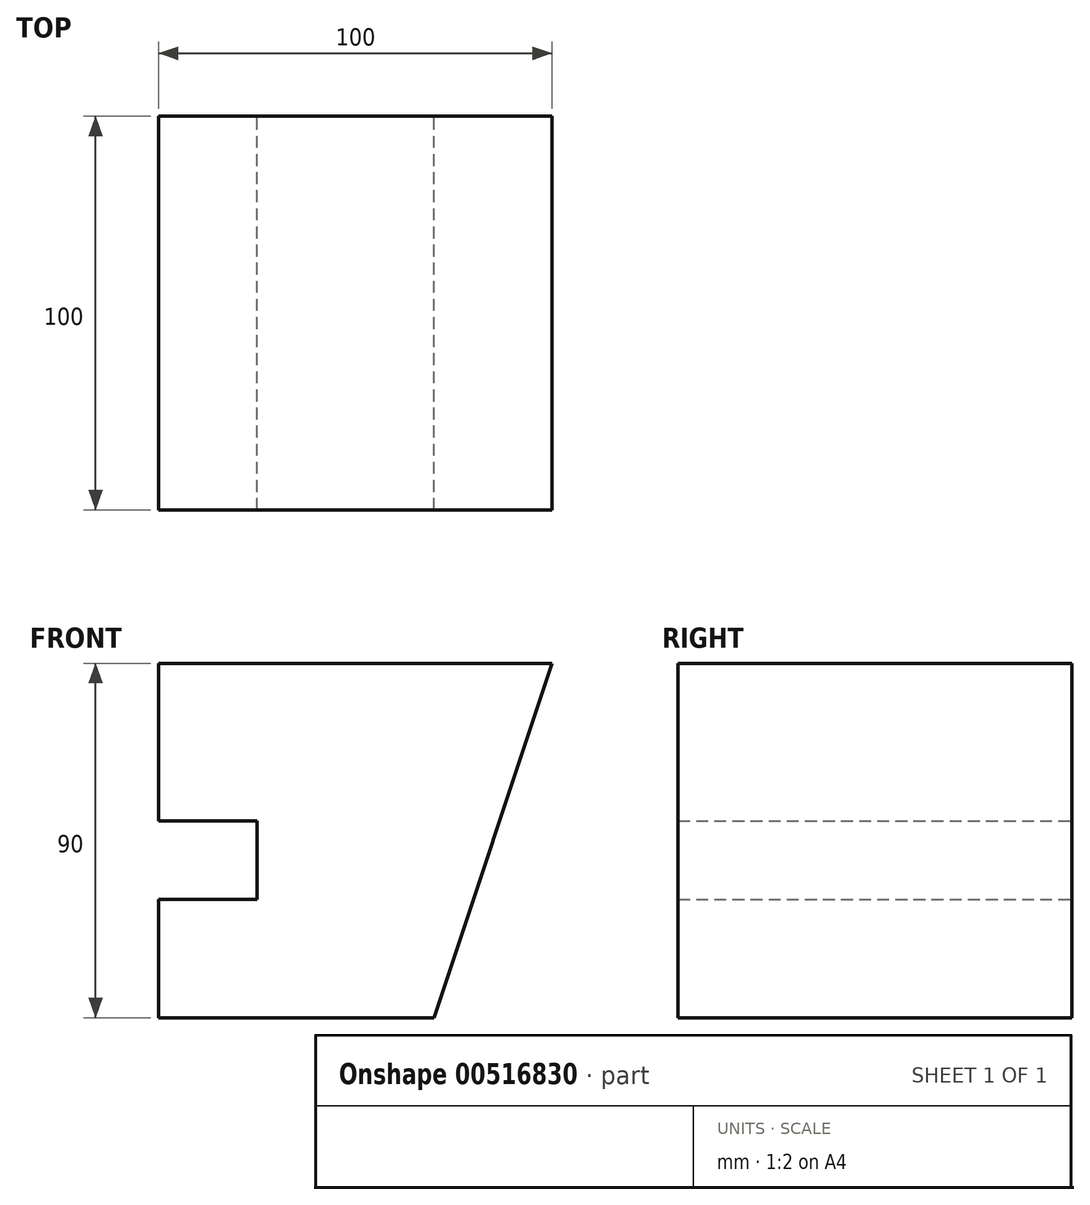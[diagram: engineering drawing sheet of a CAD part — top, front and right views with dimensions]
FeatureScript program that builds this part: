
annotation { "Feature Type Name" : "Feature", "Feature Type Description" : "" }
export const myFeature = defineFeature(function(context is Context, id is Id, definition is map)
    precondition{}
    {
        {
            var Q0;
            Q0=qCreatedBy(makeId("Front.planeOp"),FACE);
            var sketch = newSketch(context, id + "F0", { "sketchPlane" : qUnion([Q0])});
            skLineSegment(sketch, "E0", {"start": v(0, 0) * mm, "end": v(70, 0) * mm});
            skLineSegment(sketch, "E1", {"start": v(70, 0) * mm, "end": v(100, 90) * mm});
            skLineSegment(sketch, "E2", {"start": v(100, 90) * mm, "end": v(0, 90) * mm});
            skLineSegment(sketch, "E3", {"start": v(0, 90) * mm, "end": v(0, 50) * mm});
            skLineSegment(sketch, "E4", {"start": v(0, 50) * mm, "end": v(25, 50) * mm});
            skLineSegment(sketch, "E5", {"start": v(25, 50) * mm, "end": v(25, 30) * mm});
            skLineSegment(sketch, "E6", {"start": v(25, 30) * mm, "end": v(0, 30) * mm});
            skLineSegment(sketch, "E7", {"start": v(0, 30) * mm, "end": v(0, 0) * mm});
            skSolve(sketch);
        }
        {
            var Q0;
            Q0 = qSketchRegion(id + "F0", true);
            extrude(context, id + "F1", {"entities" : qUnion([Q0]), "depth" : 100 * mm, "offsetDistance" : 25 * mm});
        }
    });
